# Revit family: Elbow_Copper-90
name_source: partatom
category: Plumbing Fixtures
units: mm (PartAtom-declared; Revit-internal decimal feet)

## family parameters
Always vertical = Yes
Classification Number = 23.60.30.11.14
Cut with Voids When Loaded = No
Enable Cutting in Views = No
Maintain Annotation Orientation = No
Part Type = Normal
Room Calculation Point = No
Round Connector Dimension = Use Diameter
Shared = No
Work Plane-Based = Yes

## types (5) — shared parameters
Assembly Code = D2090900
CW Connection = Yes
Collar Thickness = 0' - 0 3/32"
Construction Details = http://www.arcat.com
Default Elevation = 4' - 0"
Description = 90 Degree Copper Sweat Elbow
Expected Lifespan (Years) = 40
Green Building-LEED = http://www.arcat.com
HW Connection = Yes
Keynote = 15000
Manufacturer = Generic
Manufacturer Fax = (203) 939-2444
Manufacturer Website = http://www.arcat.com
Model = Generic
Pipe Material = ARCAT - Copper
Product Data = http://www.arcat.com
Product Properties = http://www.arcat.com
Specification = http://www.arcat.com
Vent Connection = No
Wall Thickness = 0' - 0 1/16"
Waste Connection = No
zero-valued in all types: Maintenance Schedule (Months), Warranty Duration (Years)

## per-type parameters (varying)
| type | Supply Connection Type |
| 1" | Plumbing-Connector : Sweat-Sweat -C-C 1 |
| 1-1/4" | Plumbing-Connector : Sweat-Sweat -C-C 125 |
| 3/8" | Plumbing-Connector : Sweat-Sweat -C-C 0375 |
| 1/2" | Plumbing-Connector : Sweat-Sweat -C-C 050 |
| 3/4" | Plumbing-Connector : Sweat-Sweat -C-C 075 |

## geometry (parser evidence)
native form markers: Sweep x5
no freeform markers — native parametric forms only
